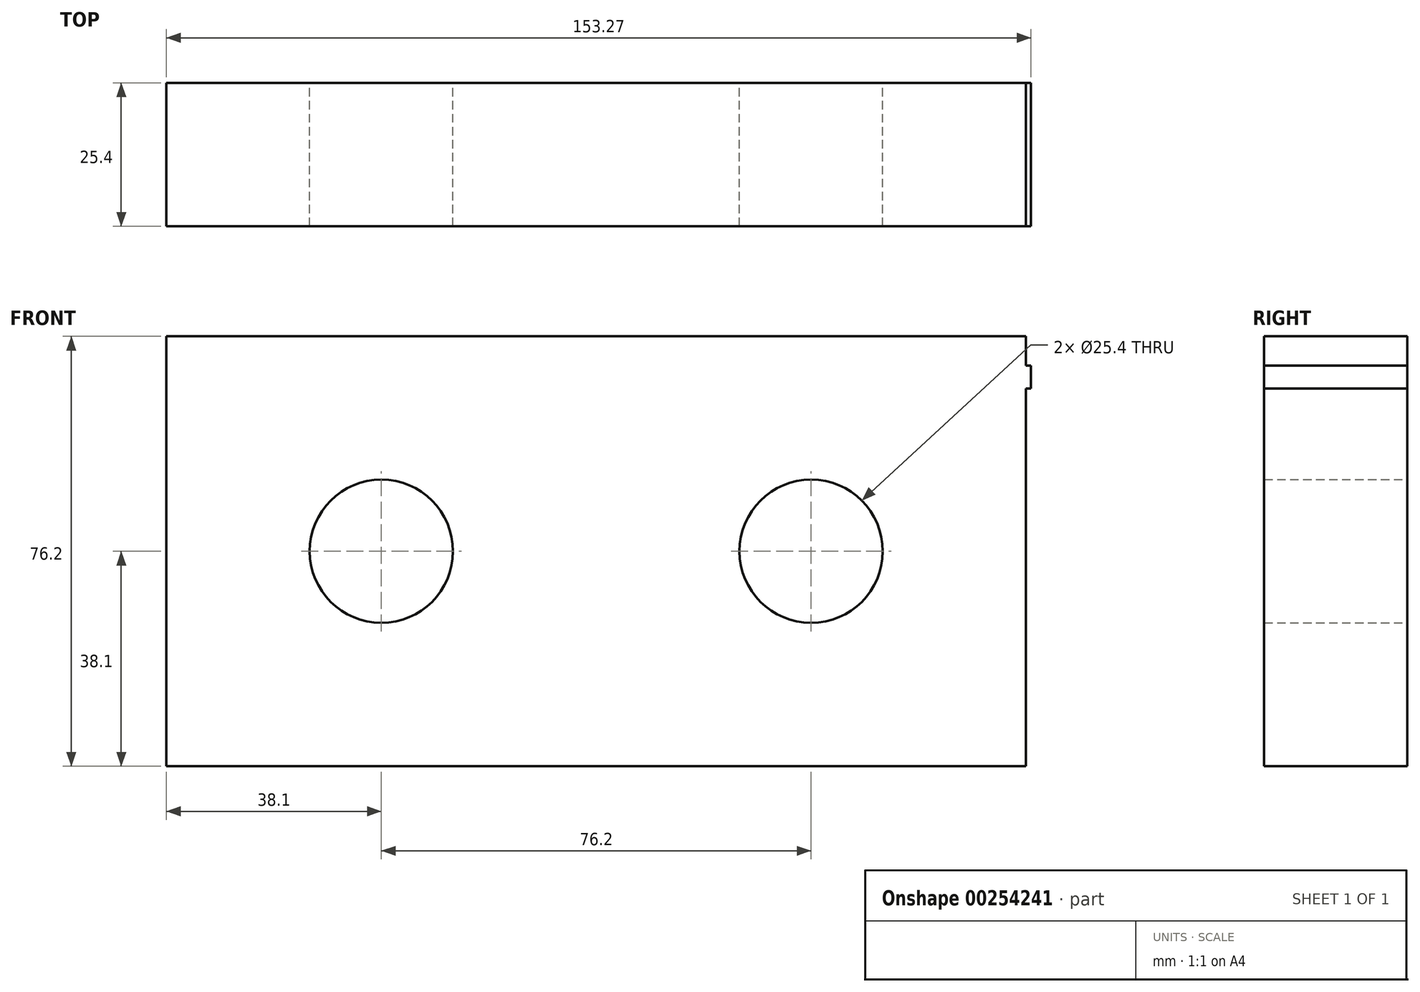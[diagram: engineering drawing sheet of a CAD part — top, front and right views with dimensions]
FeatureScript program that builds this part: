
annotation { "Feature Type Name" : "Feature", "Feature Type Description" : "" }
export const myFeature = defineFeature(function(context is Context, id is Id, definition is map)
    precondition{}
    {
        {
            var Q0;
            Q0=qCreatedBy(makeId("Front.planeOp"),FACE);
            var sketch = newSketch(context, id + "F0", { "sketchPlane" : qUnion([Q0])});
            skLineSegment(sketch, "E0.bottom", {"start": v(76.2, 38.1) * mm, "end": v(-76.2, 38.1) * mm});
            skLineSegment(sketch, "E0.top", {"start": v(76.2, -38.1) * mm, "end": v(-76.2, -38.1) * mm});
            skLineSegment(sketch, "E0.left", {"start": v(76.2, 38.1) * mm, "end": v(76.2, -38.1) * mm});
            skLineSegment(sketch, "E0.right", {"start": v(-76.2, 38.1) * mm, "end": v(-76.2, -38.1) * mm});
            skPoint(sketch, "E0.middle", {"position": v(0, 0) * mm});
            skLineSegment(sketch, "E1.bottom", {"start": v(77.07, 32.88) * mm, "end": v(75.33, 32.88) * mm});
            skLineSegment(sketch, "E1.top", {"start": v(77.07, 28.83) * mm, "end": v(75.33, 28.83) * mm});
            skLineSegment(sketch, "E1.left", {"start": v(77.07, 32.88) * mm, "end": v(77.07, 28.83) * mm});
            skLineSegment(sketch, "E1.right", {"start": v(75.33, 32.88) * mm, "end": v(75.33, 28.83) * mm});
            skPoint(sketch, "E1.middle", {"position": v(76.2, 30.86) * mm});
            skLineSegment(sketch, "E2", {"start": v(0, 0) * mm, "end": v(-38.1, 0) * mm});
            skCircle(sketch, "E3", {"center": v(-38.1, 0) * mm, "radius": 12.7 * mm});
            skLineSegment(sketch, "E4", {"start": v(0, 0) * mm, "end": v(38.1, 0) * mm});
            skCircle(sketch, "E5", {"center": v(38.1, 0) * mm, "radius": 12.7 * mm});
            skSolve(sketch);
        }
        {
            var Q0;
            Q0 = qSketchRegion(id + "F0", true);
            extrude(context, id + "F1", {"entities" : qUnion([Q0]), "depth" : 25.4 * mm});
        }
    });
